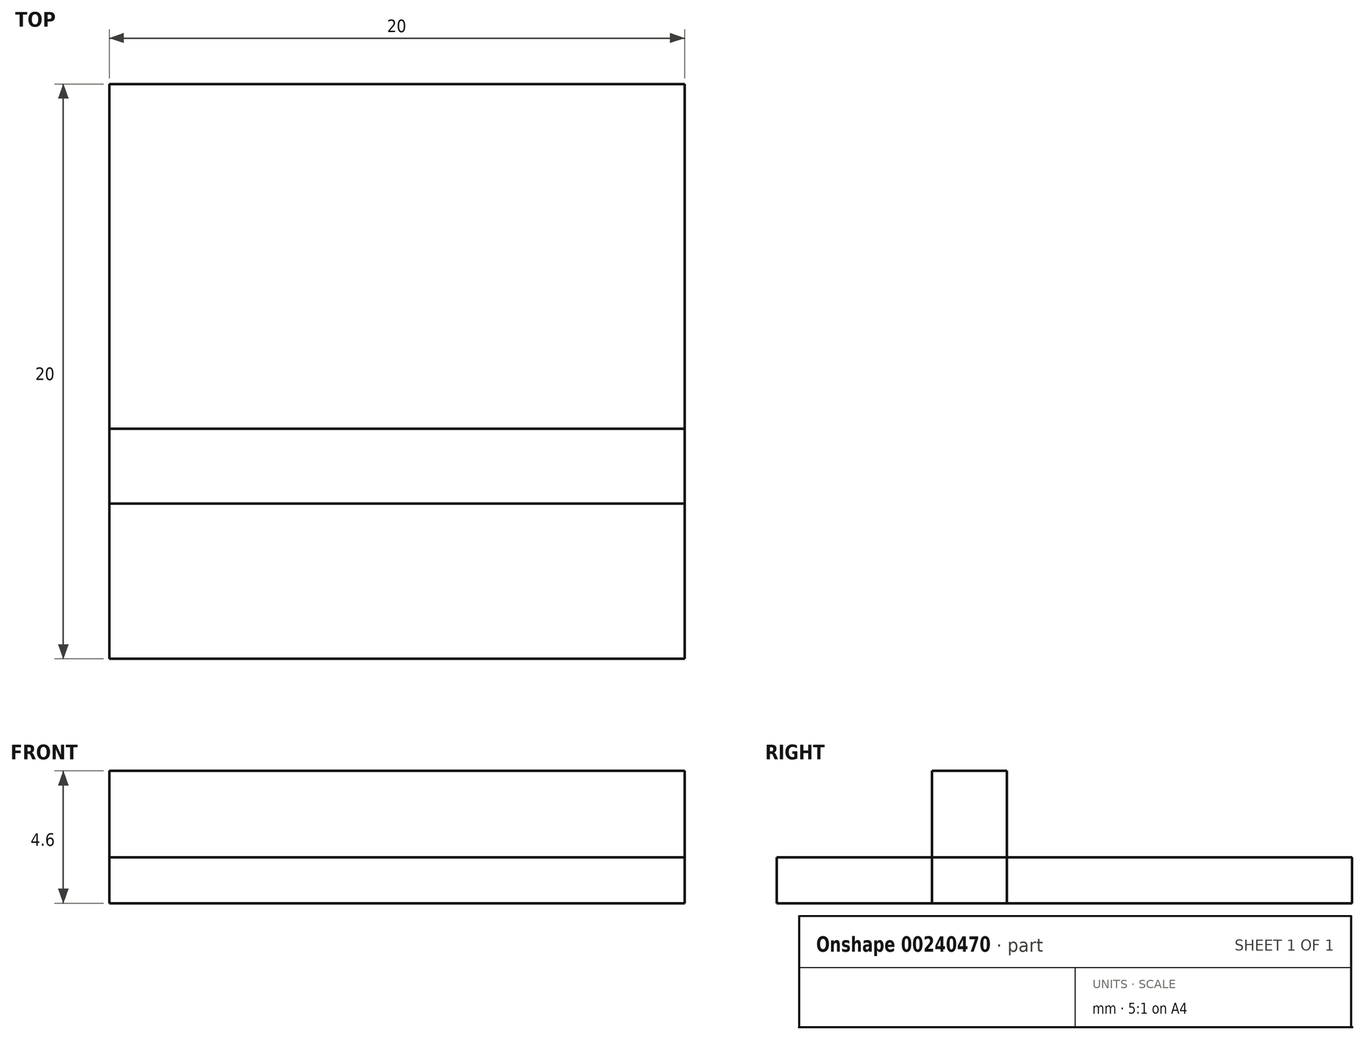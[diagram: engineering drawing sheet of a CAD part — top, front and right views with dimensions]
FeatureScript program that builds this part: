
annotation { "Feature Type Name" : "Feature", "Feature Type Description" : "" }
export const myFeature = defineFeature(function(context is Context, id is Id, definition is map)
    precondition{}
    {
        {
            var Q0;
            Q0=qCreatedBy(makeId("Top.planeOp"),FACE);
            var sketch = newSketch(context, id + "F0", { "sketchPlane" : qUnion([Q0])});
            skLineSegment(sketch, "E0.bottom", {"start": v(10, -10) * mm, "end": v(-10, -10) * mm});
            skLineSegment(sketch, "E0.top", {"start": v(10, 10) * mm, "end": v(-10, 10) * mm});
            skLineSegment(sketch, "E0.left", {"start": v(10, -10) * mm, "end": v(10, 10) * mm});
            skLineSegment(sketch, "E0.right", {"start": v(-10, -10) * mm, "end": v(-10, 10) * mm});
            skPoint(sketch, "E0.middle", {"position": v(0, 0) * mm});
            skSolve(sketch);
        }
        {
            var Q0;
            Q0 = qSketchRegion(id + "F0", true);
            extrude(context, id + "F1", {"entities" : qUnion([Q0]), "depth" : 1.6 * mm});
        }
        {
            var Q0;
            Q0=qCreatedBy(makeId("Top.planeOp"),FACE);
            var sketch = newSketch(context, id + "F2", { "sketchPlane" : qUnion([Q0])});
            skLineSegment(sketch, "E1", {"start": v(0, -4.6) * mm, "end": v(10, -4.6) * mm});
            skLineSegment(sketch, "E2", {"start": v(10, -4.6) * mm, "end": v(10, -2) * mm});
            skLineSegment(sketch, "E3", {"start": v(10, -2) * mm, "end": v(-10, -2) * mm});
            skLineSegment(sketch, "E4", {"start": v(-10, -2) * mm, "end": v(-10, -4.6) * mm});
            skLineSegment(sketch, "E5", {"start": v(-10, -4.6) * mm, "end": v(0, -4.6) * mm});
            skPoint(sketch, "E6.end.orphan", {"position": v(0, -2) * mm});
            skSolve(sketch);
        }
        {
            var Q0;
            Q0 = qSketchRegion(id + "F2", true);
            extrude(context, id + "F3", {"entities" : qUnion([Q0]), "depth" : 4.6 * mm});
        }
    });
